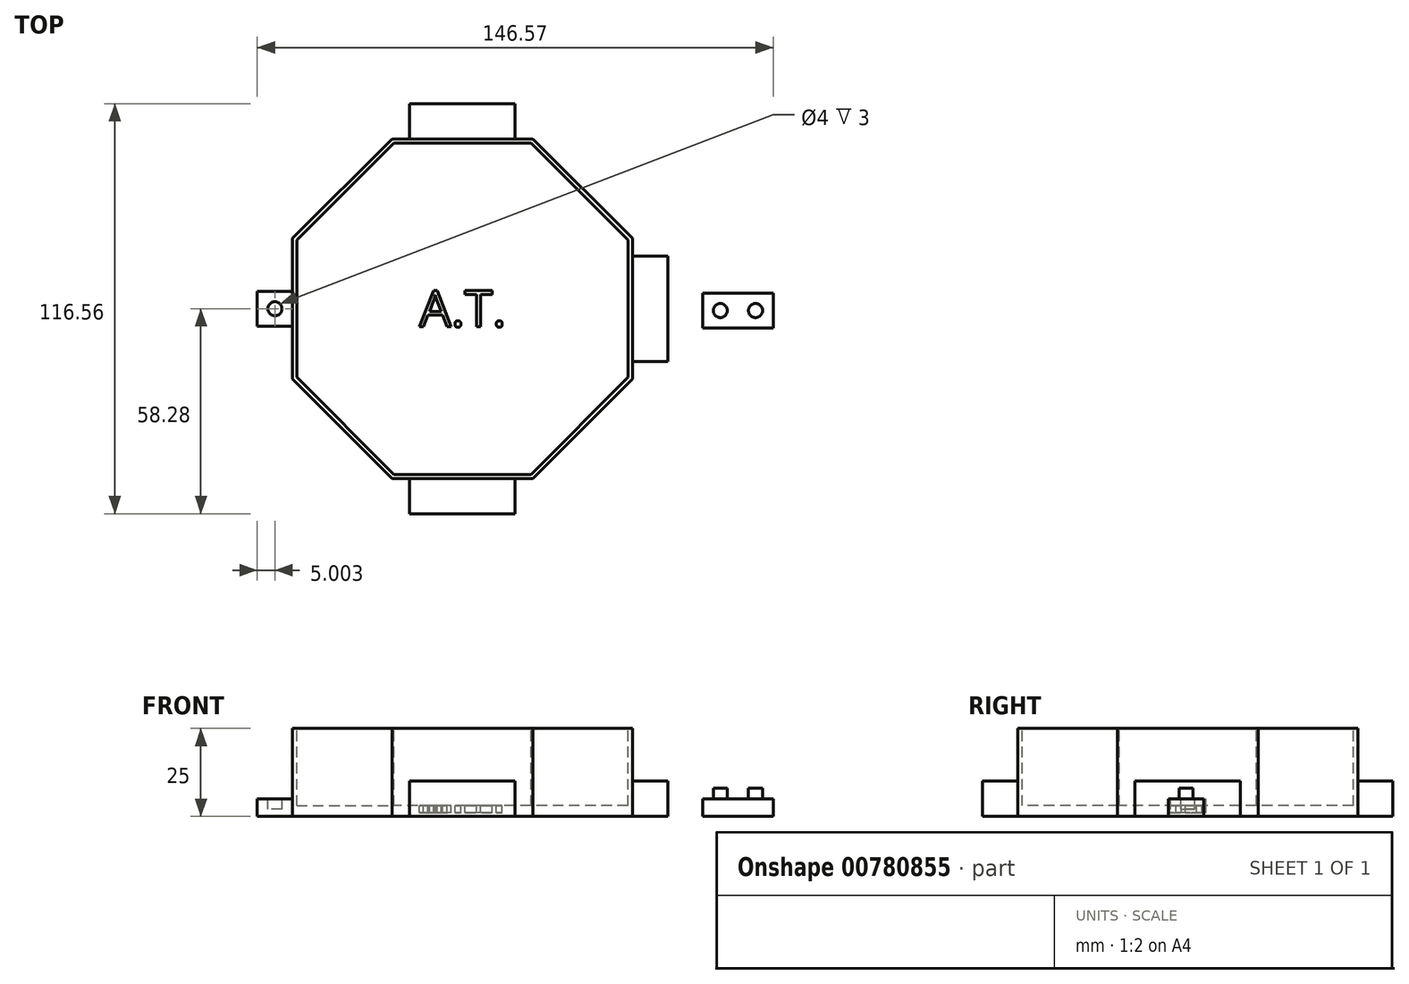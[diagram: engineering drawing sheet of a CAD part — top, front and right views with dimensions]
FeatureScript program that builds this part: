
annotation { "Feature Type Name" : "Feature", "Feature Type Description" : "" }
export const myFeature = defineFeature(function(context is Context, id is Id, definition is map)
    precondition{}
    {
        {
            var Q0;
            Q0=qCreatedBy(makeId("Top.planeOp"),FACE);
            var sketch = newSketch(context, id + "F0", { "sketchPlane" : qUnion([Q0])});
            skLineSegment(sketch, "E0.bottom", {"start": v(-3.99, 4.5) * mm, "end": v(16.01, 4.5) * mm});
            skLineSegment(sketch, "E0.top", {"start": v(-3.99, -5.5) * mm, "end": v(16.01, -5.5) * mm});
            skLineSegment(sketch, "E0.left", {"start": v(-3.99, 4.5) * mm, "end": v(-3.99, -5.5) * mm});
            skLineSegment(sketch, "E0.right", {"start": v(16.01, 4.5) * mm, "end": v(16.01, -5.5) * mm});
            skSolve(sketch);
        }
        {
            var Q0;
            Q0=makeQuery(id+"F0.imprint","IMPRINT",FACE,{"disambiguationData":[TD([[makeQuery(id+"F0.imprint","IMPRINT",EDGE,{"derivedFrom":sQuery(id+"F0.wireOp",EDGE,"E0.bottom")}),-1.0]])]});
            extrude(context, id + "F1", {"entities" : qUnion([Q0]), "depth" : 5 * mm, "offsetDistance" : 25 * mm});
        }
        {
            var Q0;
            Q0=makeQuery(id+"F1.opExtrude","CAP_FACE",FACE,{"disambiguationData":[OSD([sQuery(id+"F0.wireOp",EDGE,"E0.bottom"),sQuery(id+"F0.wireOp",EDGE,"E0.top"),sQuery(id+"F0.wireOp",EDGE,"E0.left"),sQuery(id+"F0.wireOp",EDGE,"E0.right")])],"isStart":false});
            var sketch = newSketch(context, id + "F2", { "sketchPlane" : qUnion([Q0])});
            skCircle(sketch, "E1", {"center": v(1.01, -0.5) * mm, "radius": 2 * mm});
            skCircle(sketch, "E2", {"center": v(11.01, -0.5) * mm, "radius": 2 * mm});
            skSolve(sketch);
        }
        {
            var Q0;
            Q0 = qSketchRegion(id + "F2", true);
            extrude(context, id + "F3", {"entities" : qUnion([Q0]), "operationType" : NewBodyOperationType.ADD, "depth" : 3 * mm, "offsetDistance" : 25 * mm});
        }
        {
            var Q0;
            Q0=qCreatedBy(makeId("Top.planeOp"),FACE);
            var sketch = newSketch(context, id + "F4", { "sketchPlane" : qUnion([Q0])});
            skCircle(sketch, "E3.cCircle", {"center": v(-72.27, 0) * mm, "radius": 48.28 * mm, "construction": true});
            skLineSegment(sketch, "E3.0", {"start": v(-23.99, -20) * mm, "end": v(-52.27, -48.28) * mm});
            skLineSegment(sketch, "E3.1", {"start": v(-52.27, -48.28) * mm, "end": v(-92.27, -48.28) * mm});
            skLineSegment(sketch, "E3.2", {"start": v(-92.27, -48.28) * mm, "end": v(-120.56, -20) * mm});
            skLineSegment(sketch, "E3.3", {"start": v(-120.56, -20) * mm, "end": v(-120.56, 20) * mm});
            skLineSegment(sketch, "E3.4", {"start": v(-120.56, 20) * mm, "end": v(-92.27, 48.28) * mm});
            skLineSegment(sketch, "E3.5", {"start": v(-92.27, 48.28) * mm, "end": v(-52.27, 48.28) * mm});
            skLineSegment(sketch, "E3.6", {"start": v(-52.27, 48.28) * mm, "end": v(-23.99, 20) * mm});
            skLineSegment(sketch, "E3.7", {"start": v(-23.99, 20) * mm, "end": v(-23.99, -20) * mm});
            skPoint(sketch, "E3.0.midPoint", {"position": v(-38.13, -34.14) * mm});
            skLineSegment(sketch, "E4.bottom", {"start": v(-130.56, 5) * mm, "end": v(-120.56, 5) * mm});
            skLineSegment(sketch, "E4.top", {"start": v(-130.56, -5) * mm, "end": v(-120.56, -5) * mm});
            skLineSegment(sketch, "E4.left", {"start": v(-130.56, 5) * mm, "end": v(-130.56, -5) * mm});
            skLineSegment(sketch, "E4.right", {"start": v(-120.56, 5) * mm, "end": v(-120.56, -5) * mm});
            skLineSegment(sketch, "E5.right", {"start": v(-120.56, -1.05) * mm, "end": v(-120.56, -11.05) * mm});
            skSolve(sketch);
        }
        {
            var Q0;
            Q0=makeQuery(id+"F4.imprint","IMPRINT",FACE,{"disambiguationData":[TD([[makeQuery(id+"F4.imprint","IMPRINT",EDGE,{"derivedFrom":sQuery(id+"F4.wireOp",EDGE,"E3.0")}),-1.0]])]});
            extrude(context, id + "F5", {"entities" : qUnion([Q0]), "depth" : 25 * mm, "offsetDistance" : 25 * mm});
        }
        {
            var Q0;
            Q0=makeQuery(id+"F4.imprint","IMPRINT",FACE,{"disambiguationData":[TD([[makeQuery(id+"F4.imprint","IMPRINT",EDGE,{"derivedFrom":sQuery(id+"F4.wireOp",EDGE,"E4.bottom")}),-1.0]])]});
            extrude(context, id + "F6", {"entities" : qUnion([Q0]), "operationType" : NewBodyOperationType.ADD, "depth" : 5 * mm, "offsetDistance" : 25 * mm});
        }
        {
            var Q0;
            Q0=makeQuery(id+"F6.opExtrude","CAP_FACE",FACE,{"disambiguationData":[OSD([sQuery(id+"F4.wireOp",EDGE,"E4.bottom"),sQuery(id+"F4.wireOp",EDGE,"E4.top"),sQuery(id+"F4.wireOp",EDGE,"E4.left"),sQuery(id+"F4.wireOp",EDGE,"E4.right"),sQuery(id+"F4.wireOp",EDGE,"E5.right")])],"isStart":false});
            var sketch = newSketch(context, id + "F7", { "sketchPlane" : qUnion([Q0])});
            skCircle(sketch, "E6", {"center": v(-125.56, 0) * mm, "radius": 2 * mm});
            skSolve(sketch);
        }
        {
            var Q0;
            Q0=makeQuery(id+"F7.imprint","IMPRINT",FACE,{"disambiguationData":[TD([[makeQuery(id+"F7.imprint","IMPRINT",EDGE,{"derivedFrom":sQuery(id+"F7.wireOp",EDGE,"E6")}),1.0]])]});
            extrude(context, id + "F8", {"entities" : qUnion([Q0]), "operationType" : NewBodyOperationType.REMOVE, "oppositeDirection" : true, "depth" : 3 * mm, "offsetDistance" : 25 * mm});
        }
        {
            var Q0;
            Q0=makeQuery(id+"F5.opExtrude","SWEPT_FACE",FACE,{"disambiguationData":[OSD([sQuery(id+"F4.wireOp",EDGE,"E3.1")])]});
            var sketch = newSketch(context, id + "F9", { "sketchPlane" : qUnion([Q0])});
            skLineSegment(sketch, "E7.bottom", {"start": v(-87.27, 0) * mm, "end": v(-57.27, 0) * mm});
            skLineSegment(sketch, "E7.top", {"start": v(-87.27, 10) * mm, "end": v(-57.27, 10) * mm});
            skLineSegment(sketch, "E7.left", {"start": v(-87.27, 0) * mm, "end": v(-87.27, 10) * mm});
            skLineSegment(sketch, "E7.right", {"start": v(-57.27, 0) * mm, "end": v(-57.27, 10) * mm});
            skSolve(sketch);
        }
        {
            var Q0;
            Q0=makeQuery(id+"F5.opExtrude","SWEPT_FACE",FACE,{"disambiguationData":[OSD([sQuery(id+"F4.wireOp",EDGE,"E3.7")])]});
            var sketch = newSketch(context, id + "F10", { "sketchPlane" : qUnion([Q0])});
            skLineSegment(sketch, "E8.bottom", {"start": v(-15, 0) * mm, "end": v(15, 0) * mm});
            skLineSegment(sketch, "E8.top", {"start": v(-15, 10) * mm, "end": v(15, 10) * mm});
            skLineSegment(sketch, "E8.left", {"start": v(-15, 0) * mm, "end": v(-15, 10) * mm});
            skLineSegment(sketch, "E8.right", {"start": v(15, 0) * mm, "end": v(15, 10) * mm});
            skSolve(sketch);
        }
        {
            var Q0;
            Q0=makeQuery(id+"F5.opExtrude","SWEPT_FACE",FACE,{"disambiguationData":[OSD([sQuery(id+"F4.wireOp",EDGE,"E3.5")])]});
            var sketch = newSketch(context, id + "F11", { "sketchPlane" : qUnion([Q0])});
            skLineSegment(sketch, "E9.bottom", {"start": v(57.27, 0) * mm, "end": v(87.27, 0) * mm});
            skLineSegment(sketch, "E9.top", {"start": v(57.27, 10) * mm, "end": v(87.27, 10) * mm});
            skLineSegment(sketch, "E9.left", {"start": v(57.27, 0) * mm, "end": v(57.27, 10) * mm});
            skLineSegment(sketch, "E9.right", {"start": v(87.27, 0) * mm, "end": v(87.27, 10) * mm});
            skSolve(sketch);
        }
        {
            var Q0;
            Q0=makeQuery(id+"F11.imprint","IMPRINT",FACE,{"disambiguationData":[TD([[makeQuery(id+"F11.imprint","IMPRINT",EDGE,{"derivedFrom":sQuery(id+"F11.wireOp",EDGE,"E9.bottom")}),-1.0]])]});
            extrude(context, id + "F12", {"entities" : qUnion([Q0]), "operationType" : NewBodyOperationType.ADD, "depth" : 10 * mm, "offsetDistance" : 25 * mm});
        }
        {
            var Q0;
            Q0=makeQuery(id+"F10.imprint","IMPRINT",FACE,{"disambiguationData":[TD([[makeQuery(id+"F10.imprint","IMPRINT",EDGE,{"derivedFrom":sQuery(id+"F10.wireOp",EDGE,"E8.bottom")}),-1.0]])]});
            extrude(context, id + "F13", {"entities" : qUnion([Q0]), "operationType" : NewBodyOperationType.ADD, "depth" : 10.1 * mm, "offsetDistance" : 25 * mm});
        }
        {
            var Q0;
            Q0=makeQuery(id+"F9.imprint","IMPRINT",FACE,{"disambiguationData":[TD([[makeQuery(id+"F9.imprint","IMPRINT",EDGE,{"derivedFrom":sQuery(id+"F9.wireOp",EDGE,"E7.bottom")}),-1.0]])]});
            extrude(context, id + "F14", {"entities" : qUnion([Q0]), "operationType" : NewBodyOperationType.ADD, "depth" : 10 * mm, "offsetDistance" : 25 * mm});
        }
        {
            var Q0;
            Q0=makeQuery(id+"F5.opExtrude","CAP_FACE",FACE,{"disambiguationData":[OSD([sQuery(id+"F4.wireOp",EDGE,"E3.0"),sQuery(id+"F4.wireOp",EDGE,"E3.1"),sQuery(id+"F4.wireOp",EDGE,"E3.2"),sQuery(id+"F4.wireOp",EDGE,"E3.3"),sQuery(id+"F4.wireOp",EDGE,"E3.4"),sQuery(id+"F4.wireOp",EDGE,"E3.5"),sQuery(id+"F4.wireOp",EDGE,"E3.6"),sQuery(id+"F4.wireOp",EDGE,"E3.7"),sQuery(id+"F4.wireOp",EDGE,"E4.right"),sQuery(id+"F4.wireOp",EDGE,"E5.right")])],"isStart":false});
            var sketch = newSketch(context, id + "F15", { "sketchPlane" : qUnion([Q0])});
            skCircle(sketch, "E10.cCircle", {"center": v(-72.27, 0) * mm, "radius": 47.08 * mm, "construction": true});
            skLineSegment(sketch, "E10.0", {"start": v(-52.77, -47.08) * mm, "end": v(-91.77, -47.08) * mm});
            skLineSegment(sketch, "E10.1", {"start": v(-91.77, -47.08) * mm, "end": v(-119.35, -19.5) * mm});
            skLineSegment(sketch, "E10.2", {"start": v(-119.35, -19.5) * mm, "end": v(-119.35, 19.5) * mm});
            skLineSegment(sketch, "E10.3", {"start": v(-119.35, 19.5) * mm, "end": v(-91.77, 47.08) * mm});
            skLineSegment(sketch, "E10.4", {"start": v(-91.77, 47.08) * mm, "end": v(-52.77, 47.08) * mm});
            skLineSegment(sketch, "E10.5", {"start": v(-52.77, 47.08) * mm, "end": v(-25.2, 19.5) * mm});
            skLineSegment(sketch, "E10.6", {"start": v(-25.2, 19.5) * mm, "end": v(-25.2, -19.5) * mm});
            skLineSegment(sketch, "E10.7", {"start": v(-25.2, -19.5) * mm, "end": v(-52.77, -47.08) * mm});
            skPoint(sketch, "E10.0.midPoint", {"position": v(-72.27, -47.08) * mm});
            skSolve(sketch);
        }
        {
            var Q0;
            Q0=makeQuery(id+"F15.imprint","IMPRINT",FACE,{"disambiguationData":[TD([[makeQuery(id+"F15.imprint","IMPRINT",EDGE,{"derivedFrom":sQuery(id+"F15.wireOp",EDGE,"E10.0")}),-1.0]])]});
            extrude(context, id + "F16", {"entities" : qUnion([Q0]), "operationType" : NewBodyOperationType.REMOVE, "oppositeDirection" : true, "depth" : 22 * mm, "offsetDistance" : 25 * mm});
        }
        {
            var Q0;
            Q0=makeQuery(id+"F16.boolean.opBoolean","COPY",FACE,{"derivedFrom":makeQuery(id+"F16.opExtrude","CAP_FACE",FACE,{"disambiguationData":[OSD([sQuery(id+"F15.wireOp",EDGE,"E10.0"),sQuery(id+"F15.wireOp",EDGE,"E10.1"),sQuery(id+"F15.wireOp",EDGE,"E10.2"),sQuery(id+"F15.wireOp",EDGE,"E10.3"),sQuery(id+"F15.wireOp",EDGE,"E10.4"),sQuery(id+"F15.wireOp",EDGE,"E10.5"),sQuery(id+"F15.wireOp",EDGE,"E10.6"),sQuery(id+"F15.wireOp",EDGE,"E10.7")])],"isStart":false})});
            var sketch = newSketch(context, id + "F17", { "sketchPlane" : qUnion([Q0])});
            skText(sketch, "E11", { "text": "A.T.", "fontName": "OpenSans-Regular.ttf"});
            const initialGuessF17  = {"E11": [-0.08452, -0.00507, 1, 0, 0.01032]};
            skSetInitialGuess(sketch, initialGuessF17);
            skSolve(sketch);
        }
        {
            var Q0;
            Q0 = qSketchRegion(id + "F17", true);
            extrude(context, id + "F18", {"entities" : qUnion([Q0]), "operationType" : NewBodyOperationType.REMOVE, "oppositeDirection" : true, "depth" : 2 * mm, "offsetDistance" : 25 * mm});
        }
    });
